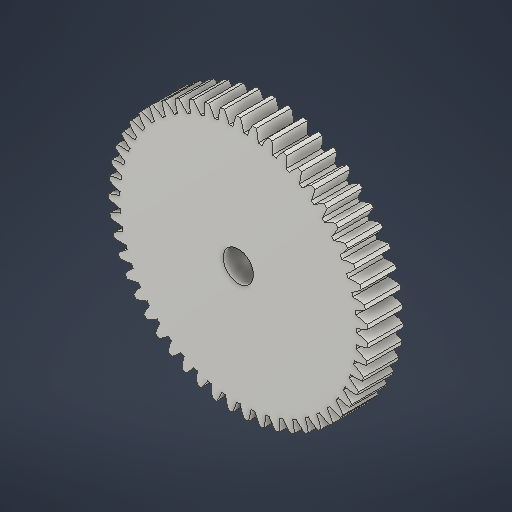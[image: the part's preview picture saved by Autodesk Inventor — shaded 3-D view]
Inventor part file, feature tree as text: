
AUTODESK INVENTOR PART (.ipt)
format: ipt  version: 2025.3 (Build 293356030, 356C)  size: 444,416 bytes
history: native  units: mm (DEFAULTED — no unit token found)
features: plane x3, other x3, extrude x2, sketch x2
ambient origin geometry x8: Origin, YZ Plane, XZ Plane, XY Plane, X Axis, Y Axis, Z Axis, Center Point
bodies: Solid1 (feature_tree)
feature tree (10):
  extrude  "Extrusion1"  Depth=8.0mm TaperAngle=0.0deg
  plane  "Work Plane2"
  plane  "Work Plane8"
  plane  "Work Plane9"
  other  "Spur Gear"
  extrude  "Extrusion2"  Depth=10.0mm TaperAngle=0.0deg
  sketch  "Sketch1"  dims[d0=58.625mm d1=8.0mm d2=0.0mm]
  other  "Srf1"
  sketch  "Sketch3"  dims[d3=57.375mm d4=10.0mm d5=0.0mm d16=40.0mm d17=0.0mm d34=0.615999mm d39=0.0mm d41=0.0mm d43=40.0mm d46=40.0mm d47=0.0mm d48=0.0mm d49=6.85mm d50=0.0mm d51=0.0mm d52=0.5mm d53=0.872665mm d54=0.5mm d55=0.872665mm]
  other  "Pitch Diameter"
